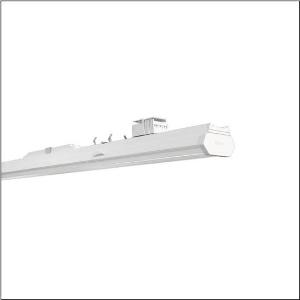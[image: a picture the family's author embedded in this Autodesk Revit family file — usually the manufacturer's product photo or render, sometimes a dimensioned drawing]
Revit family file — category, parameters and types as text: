
# Revit family: licross_r__11_protected_ho_51tp12cn4exm_ba42
name_source: partatom
category: Lighting Fixtures
units: mm (PartAtom-declared; Revit-internal decimal feet)

## family parameters
Cut with Voids When Loaded = No
Host = Face
Light Source = No
Part Type = Normal
Room Calculation Point = No
Round Connector Dimension = Use Diameter
Shared = No

## types (1)
- --- (1 x LED, 14240 lm, 77.6 W, 4000K)
    Apparent Load = 78 VA
    CIE Flux Codes = 70 91 97 98 100
    Color Rendering = 80
    Color Temperature = 4000K
    Default Elevation = 1800 mm
    Description = Licross® 11 Protected HO, luminaire insert, of sheet steel, galvanised, coil coated, white, length: 1.500mm, width: 90mm, height: 101mm, LED rated luminous flux: 14.240lm, light colour: 840, control gear: ON/OFF Multilumen, CLOi, with plug, 3-pole, with phase selection, mains connection: 220..240V, AC, 50/60Hz, start of lifetime: 78W, end of service life: 87W, halogen-free wiring, primary light control with lens, of plastic, primary optical cover: cover, of PMMA, light emission: direct distribution, primary light characteristic: symmetric, protection rating (complete): IP64, insulation class (complete): insulation class I (protective earthing), certification: CE, ENEC, VDE, UKCA, protection symbol: D if used in an environment with conductive dust loads with corresponding accessories, impact resistance: IK06, permissible ambient temperature for indoor applications: -35..+35°C, corresponds to IFS (International Featured Standards) requirements for safety and quality in the food industry, reducing of maximum allowable ambient temperature of 5°C with ceiling mounting, LABS conformity tested according to VDMA 24364:2018-05, packaging unit: 1 piece
    Height = 92 mm
    Lamp = 1 x LED
    Lamp Light Flux = 14240 lm
    Lamp Power = 77.6 W
    Lamp count = 1
    Length = 1500 mm
    Luminous efficacy = 184 lm/W
    Manufacturer = Siteco
    ModVariant = No
    Model = 51TP12CN4EXM
    Mounting Place = Ceiling
    Mounting Type = Pendant
    Number of Poles = 1
    OnlyDefault = Yes
    Power Factor = 1
    Product Name = Licross® 11 Protected HO
    Product group = luminaire insert
    ProductGroupID = 901
    Protection Class = Protection class I
    Protection Degree = IP 64
    RLX_Detail_Level = 1
    RLX_Emergency_Light_Flux = 0 lm
    RLX_Emergency_Type = 0
    RLX_Emergency_Type_DB = No
    RlxData = <blob elided: 22181 chars, md5=e31b436c>
    Socket = socket
    Standby Power = 0 W
    System Light Flux = 14240 lm
    System Power = 78 W
    Type Comments = factory setting: luminous flux: 100 % | (A | C | E) | 181 mA
    Type Image = l_1256148.jpg
    URL = http://relux.com
    VarID = @adj_055303
    Voltage = 0 V
    Weight = 0.00 kg
    Width = 88 mm

## geometry (parser evidence)
native form markers: Blend x4, Sweep x13
no freeform markers — native parametric forms only
